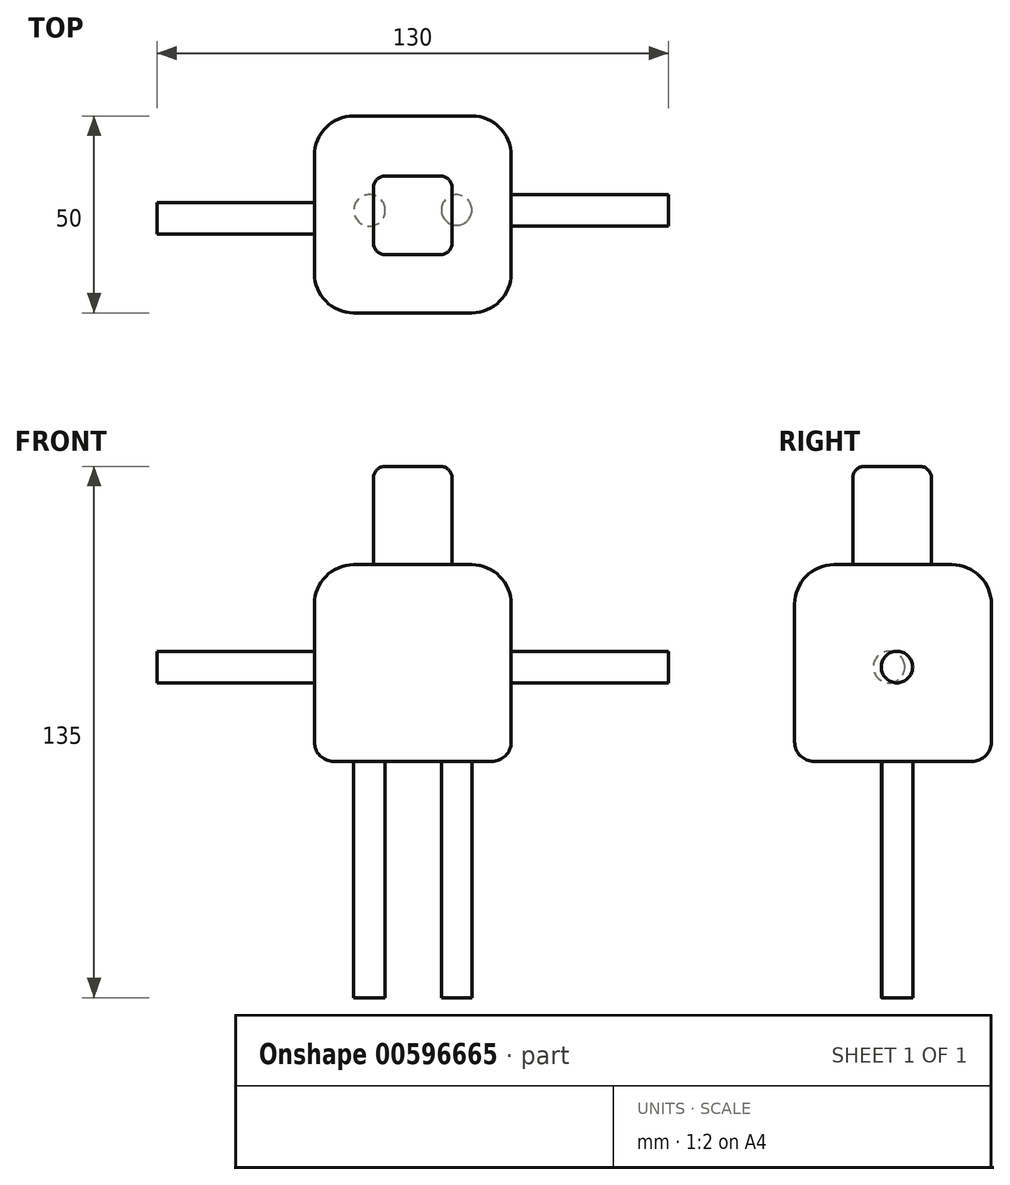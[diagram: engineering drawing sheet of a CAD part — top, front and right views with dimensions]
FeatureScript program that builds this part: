
annotation { "Feature Type Name" : "Feature", "Feature Type Description" : "" }
export const myFeature = defineFeature(function(context is Context, id is Id, definition is map)
    precondition{}
    {
        {
            var Q0;
            Q0=qCreatedBy(makeId("Top.planeOp"),FACE);
            var sketch = newSketch(context, id + "F0", { "sketchPlane" : qUnion([Q0])});
            skLineSegment(sketch, "E0.bottom", {"start": v(0, 0) * mm, "end": v(50, 0) * mm});
            skLineSegment(sketch, "E0.top", {"start": v(0, 50) * mm, "end": v(50, 50) * mm});
            skLineSegment(sketch, "E0.left", {"start": v(0, 0) * mm, "end": v(0, 50) * mm});
            skLineSegment(sketch, "E0.right", {"start": v(50, 0) * mm, "end": v(50, 50) * mm});
            skSolve(sketch);
        }
        {
            var Q0;
            Q0=makeQuery(id+"F0.imprint","IMPRINT",FACE,{"disambiguationData":[TD([[makeQuery(id+"F0.imprint","IMPRINT",EDGE,{"derivedFrom":sQuery(id+"F0.wireOp",EDGE,"E0.bottom")}),1.0]])]});
            extrude(context, id + "F1", {"entities" : qUnion([Q0]), "depth" : 50 * mm, "offsetDistance" : 25 * mm});
        }
        {
            var Q0;
            Q0=makeQuery(id+"F1.opExtrude","CAP_FACE",FACE,{"disambiguationData":[OSD([sQuery(id+"F0.wireOp",EDGE,"E0.bottom"),sQuery(id+"F0.wireOp",EDGE,"E0.top"),sQuery(id+"F0.wireOp",EDGE,"E0.left"),sQuery(id+"F0.wireOp",EDGE,"E0.right")])],"isStart":false});
            var sketch = newSketch(context, id + "F2", { "sketchPlane" : qUnion([Q0])});
            skLineSegment(sketch, "E1.bottom", {"start": v(15, 34.76) * mm, "end": v(35, 34.76) * mm});
            skLineSegment(sketch, "E1.top", {"start": v(15, 14.76) * mm, "end": v(35, 14.76) * mm});
            skLineSegment(sketch, "E1.left", {"start": v(15, 34.76) * mm, "end": v(15, 14.76) * mm});
            skLineSegment(sketch, "E1.right", {"start": v(35, 34.76) * mm, "end": v(35, 14.76) * mm});
            skSolve(sketch);
        }
        {
            var Q0;
            Q0=makeQuery(id+"F2.imprint","IMPRINT",FACE,{"disambiguationData":[TD([[makeQuery(id+"F2.imprint","IMPRINT",EDGE,{"derivedFrom":sQuery(id+"F2.wireOp",EDGE,"E1.bottom")}),-1.0]])]});
            extrude(context, id + "F3", {"entities" : qUnion([Q0]), "operationType" : NewBodyOperationType.ADD, "depth" : 25 * mm, "offsetDistance" : 25 * mm});
        }
        {
            var Q0;
            Q0=makeQuery(id+"F1.opExtrude","SWEPT_FACE",FACE,{"disambiguationData":[OSD([sQuery(id+"F0.wireOp",EDGE,"E0.right")])]});
            var sketch = newSketch(context, id + "F4", { "sketchPlane" : qUnion([Q0])});
            skCircle(sketch, "E2", {"center": v(26, 24) * mm, "radius": 4 * mm});
            skSolve(sketch);
        }
        {
            var Q0;
            Q0 = qSketchRegion(id + "F4", true);
            extrude(context, id + "F5", {"entities" : qUnion([Q0]), "operationType" : NewBodyOperationType.ADD, "depth" : 40 * mm, "offsetDistance" : 25 * mm});
        }
        {
            var Q0;
            Q0=makeQuery(id+"F1.opExtrude","SWEPT_FACE",FACE,{"disambiguationData":[OSD([sQuery(id+"F0.wireOp",EDGE,"E0.left")])]});
            var sketch = newSketch(context, id + "F6", { "sketchPlane" : qUnion([Q0])});
            skCircle(sketch, "E3", {"center": v(-24, 24) * mm, "radius": 4 * mm});
            skSolve(sketch);
        }
        {
            var Q0;
            Q0=makeQuery(id+"F6.imprint","IMPRINT",FACE,{"disambiguationData":[TD([[makeQuery(id+"F6.imprint","IMPRINT",EDGE,{"derivedFrom":sQuery(id+"F6.wireOp",EDGE,"E3")}),1.0]])]});
            extrude(context, id + "F7", {"entities" : qUnion([Q0]), "operationType" : NewBodyOperationType.ADD, "depth" : 40 * mm, "offsetDistance" : 25 * mm});
        }
        {
            var Q0;
            Q0=makeQuery(id+"F1.opExtrude","CAP_FACE",FACE,{"disambiguationData":[OSD([sQuery(id+"F0.wireOp",EDGE,"E0.bottom"),sQuery(id+"F0.wireOp",EDGE,"E0.top"),sQuery(id+"F0.wireOp",EDGE,"E0.left"),sQuery(id+"F0.wireOp",EDGE,"E0.right")])],"isStart":true});
            var sketch = newSketch(context, id + "F8", { "sketchPlane" : qUnion([Q0])});
            skCircle(sketch, "E4", {"center": v(14, -26.05) * mm, "radius": 4 * mm});
            skSolve(sketch);
        }
        {
            var Q0;
            Q0=makeQuery(id+"F8.imprint","IMPRINT",FACE,{"disambiguationData":[TD([[makeQuery(id+"F8.imprint","IMPRINT",EDGE,{"derivedFrom":sQuery(id+"F8.wireOp",EDGE,"E4")}),-1.0]])]});
            var sketch = newSketch(context, id + "F9", { "sketchPlane" : qUnion([Q0])});
            skCircle(sketch, "E5", {"center": v(36.12, -26.12) * mm, "radius": 3.88 * mm});
            skSolve(sketch);
        }
        {
            var Q0;
            Q0 = qSketchRegion(id + "F8", true);
            extrude(context, id + "F10", {"entities" : qUnion([Q0]), "operationType" : NewBodyOperationType.ADD, "depth" : 60 * mm, "offsetDistance" : 25 * mm});
        }
        {
            var Q0;
            Q0 = qSketchRegion(id + "F9", true);
            extrude(context, id + "F11", {"entities" : qUnion([Q0]), "operationType" : NewBodyOperationType.ADD, "depth" : 60 * mm, "offsetDistance" : 25 * mm});
        }
        {
            var Q0;
            Q0=makeQuery(id+"F1.opExtrude","CAP_EDGE",EDGE,{"disambiguationData":[OSD([sQuery(id+"F0.wireOp",EDGE,"E0.bottom")])],"isStart":false});
            fillet(context, id + "F12", {"entities" : qUnion([Q0]), "radius" : 10 * mm, "tangentPropagation" : true, "allowEdgeOverflow" : false});
        }
        {
            var Q0;
            Q0=makeQuery(id+"F1.opExtrude","CAP_EDGE",EDGE,{"disambiguationData":[OSD([sQuery(id+"F0.wireOp",EDGE,"E0.top")])],"isStart":false});
            fillet(context, id + "F13", {"entities" : qUnion([Q0]), "radius" : 10 * mm, "tangentPropagation" : true, "allowEdgeOverflow" : false});
        }
        {
            var Q0;
            Q0=makeQuery(id+"F1.opExtrude","CAP_EDGE",EDGE,{"disambiguationData":[OSD([sQuery(id+"F0.wireOp",EDGE,"E0.right")])],"isStart":false});
            fillet(context, id + "F14", {"entities" : qUnion([Q0]), "radius" : 10 * mm, "tangentPropagation" : true, "allowEdgeOverflow" : false});
        }
        {
            var Q0;
            Q0=makeQuery(id+"F1.opExtrude","CAP_EDGE",EDGE,{"disambiguationData":[OSD([sQuery(id+"F0.wireOp",EDGE,"E0.left")])],"isStart":false});
            fillet(context, id + "F15", {"entities" : qUnion([Q0]), "radius" : 10 * mm, "tangentPropagation" : true, "allowEdgeOverflow" : false});
        }
        {
            var Q0;
            Q0=makeQuery(id+"F3.opExtrude","CAP_EDGE",EDGE,{"disambiguationData":[OSD([sQuery(id+"F2.wireOp",EDGE,"E1.bottom")])],"isStart":false});
            var Q1;
            Q1=makeQuery(id+"F3.opExtrude","SWEPT_EDGE",EDGE,{"disambiguationData":[OSD([sQuery(id+"F2.wireOp",EDGE,"E1.bottom"),sQuery(id+"F2.wireOp",EDGE,"E1.left")])]});
            var Q2;
            Q2=makeQuery(id+"F3.opExtrude","SWEPT_EDGE",EDGE,{"disambiguationData":[OSD([sQuery(id+"F2.wireOp",EDGE,"E1.bottom"),sQuery(id+"F2.wireOp",EDGE,"E1.right")])]});
            var Q3;
            Q3=makeQuery(id+"F3.opExtrude","CAP_EDGE",EDGE,{"disambiguationData":[OSD([sQuery(id+"F2.wireOp",EDGE,"E1.left")])],"isStart":false});
            var Q4;
            Q4=makeQuery(id+"F3.opExtrude","SWEPT_EDGE",EDGE,{"disambiguationData":[OSD([sQuery(id+"F2.wireOp",EDGE,"E1.top"),sQuery(id+"F2.wireOp",EDGE,"E1.left")])]});
            var Q5;
            Q5=makeQuery(id+"F3.opExtrude","CAP_EDGE",EDGE,{"disambiguationData":[OSD([sQuery(id+"F2.wireOp",EDGE,"E1.top")])],"isStart":false});
            var Q6;
            Q6=makeQuery(id+"F3.opExtrude","SWEPT_EDGE",EDGE,{"disambiguationData":[OSD([sQuery(id+"F2.wireOp",EDGE,"E1.top"),sQuery(id+"F2.wireOp",EDGE,"E1.right")])]});
            var Q7;
            Q7=makeQuery(id+"F3.opExtrude","CAP_EDGE",EDGE,{"disambiguationData":[OSD([sQuery(id+"F2.wireOp",EDGE,"E1.right")])],"isStart":false});
            fillet(context, id + "F16", {"entities" : qUnion([Q0, Q1, Q2, Q3, Q4, Q5, Q6, Q7]), "radius" : 3 * mm, "tangentPropagation" : true, "allowEdgeOverflow" : false});
        }
        {
            var Q0;
            Q0=makeQuery(id+"F1.opExtrude","CAP_EDGE",EDGE,{"disambiguationData":[OSD([sQuery(id+"F0.wireOp",EDGE,"E0.bottom")])],"isStart":true});
            fillet(context, id + "F17", {"entities" : qUnion([Q0]), "radius" : 5 * mm, "tangentPropagation" : true, "allowEdgeOverflow" : false});
        }
    });
